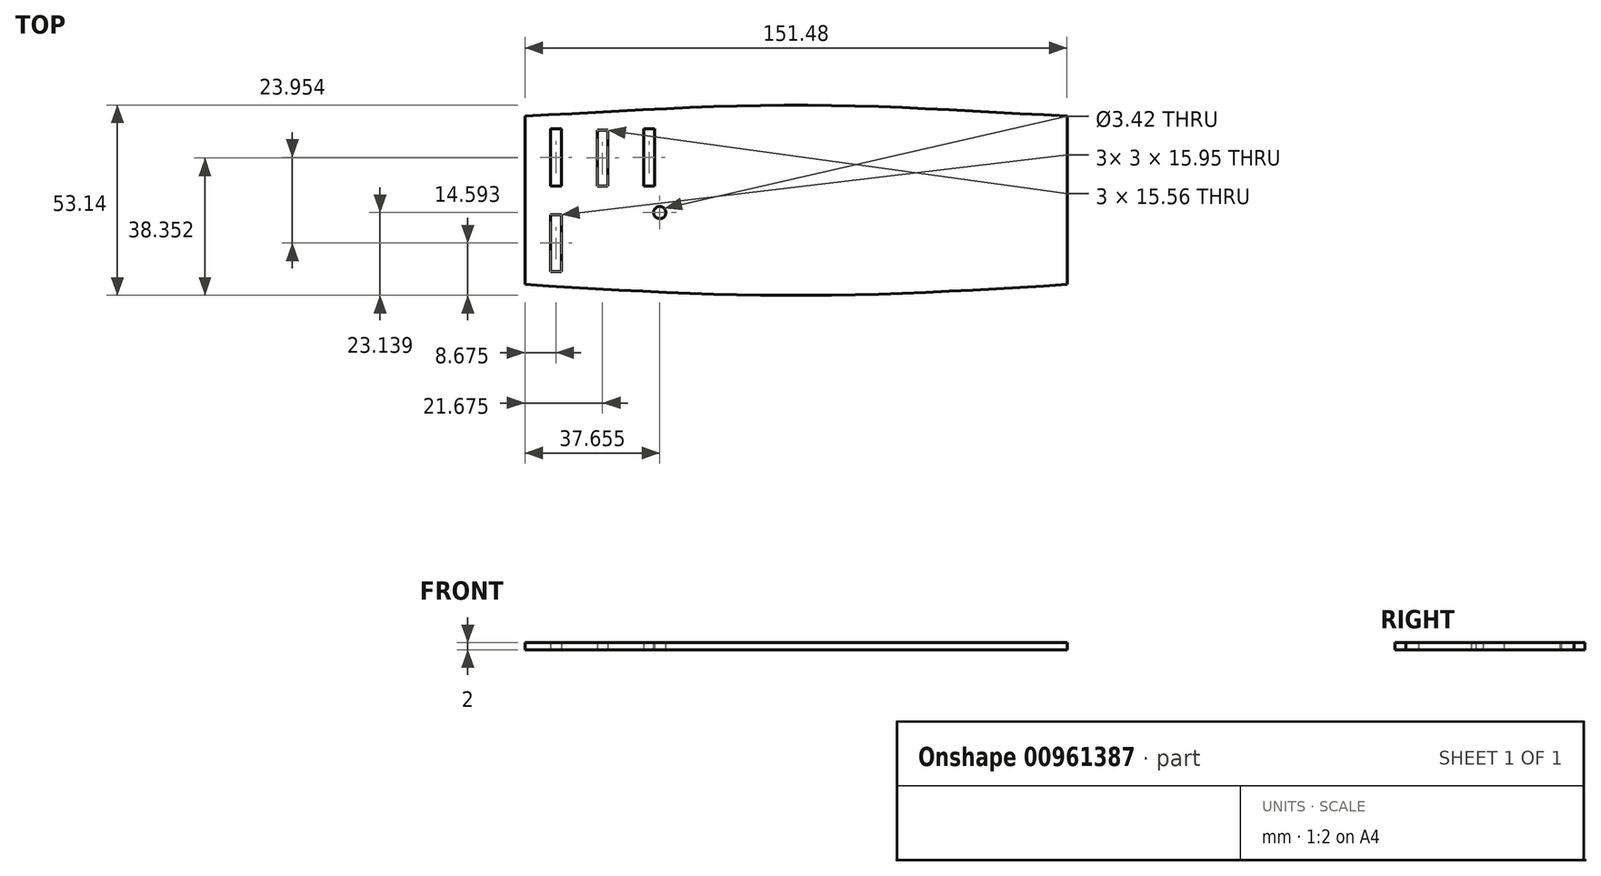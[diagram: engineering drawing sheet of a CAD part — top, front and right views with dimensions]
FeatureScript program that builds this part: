
annotation { "Feature Type Name" : "Feature", "Feature Type Description" : "" }
export const myFeature = defineFeature(function(context is Context, id is Id, definition is map)
    precondition{}
    {
        {
            var Q0;
            Q0=qCreatedBy(makeId("Top.planeOp"),FACE);
            var sketch = newSketch(context, id + "F0", { "sketchPlane" : qUnion([Q0])});
            skLineSegment(sketch, "E0.left", {"start": v(-75.74, 23.5) * mm, "end": v(-75.74, -23.5) * mm});
            skLineSegment(sketch, "E0.right", {"start": v(75.74, 23.5) * mm, "end": v(75.74, -23.5) * mm});
            skPoint(sketch, "E0.middle", {"position": v(0, 0) * mm});
            skFitSpline(sketch, "E1", {"points": [v(-75.74, -23.5) * mm, v(0, -26.57) * mm, v(75.74, -23.5) * mm], "startDerivative": vector(151.49, -9.97) * mm, "endDerivative": vector(151.49, 9.97) * mm});
            skFitSpline(sketch, "E2", {"points": [v(-75.74, 23.5) * mm, v(0, 26.57) * mm, v(75.74, 23.5) * mm], "startDerivative": vector(151.49, 7.52) * mm, "endDerivative": vector(151.49, -7.52) * mm});
            skLineSegment(sketch, "E3.bottom", {"start": v(-68.57, 19.95) * mm, "end": v(-65.57, 19.95) * mm});
            skLineSegment(sketch, "E3.top", {"start": v(-68.57, 4) * mm, "end": v(-65.57, 4) * mm});
            skLineSegment(sketch, "E3.left", {"start": v(-68.57, 19.95) * mm, "end": v(-68.57, 4) * mm});
            skLineSegment(sketch, "E3.right", {"start": v(-65.57, 19.95) * mm, "end": v(-65.57, 4) * mm});
            skLineSegment(sketch, "E4.bottom", {"start": v(-55.57, 19.56) * mm, "end": v(-52.57, 19.56) * mm});
            skLineSegment(sketch, "E4.top", {"start": v(-55.57, 4) * mm, "end": v(-52.57, 4) * mm});
            skLineSegment(sketch, "E4.left", {"start": v(-55.57, 19.56) * mm, "end": v(-55.57, 4) * mm});
            skLineSegment(sketch, "E4.right", {"start": v(-52.57, 19.56) * mm, "end": v(-52.57, 4) * mm});
            skLineSegment(sketch, "E5.bottom", {"start": v(-42.57, 19.95) * mm, "end": v(-39.57, 19.95) * mm});
            skLineSegment(sketch, "E5.top", {"start": v(-42.57, 4) * mm, "end": v(-39.57, 4) * mm});
            skLineSegment(sketch, "E5.left", {"start": v(-42.57, 19.95) * mm, "end": v(-42.57, 4) * mm});
            skLineSegment(sketch, "E5.right", {"start": v(-39.57, 19.95) * mm, "end": v(-39.57, 4) * mm});
            skLineSegment(sketch, "E6.bottom", {"start": v(-68.57, -4) * mm, "end": v(-65.57, -4) * mm});
            skLineSegment(sketch, "E6.top", {"start": v(-68.57, -19.95) * mm, "end": v(-65.57, -19.95) * mm});
            skLineSegment(sketch, "E6.left", {"start": v(-68.57, -4) * mm, "end": v(-68.57, -19.95) * mm});
            skLineSegment(sketch, "E6.right", {"start": v(-65.57, -4) * mm, "end": v(-65.57, -19.95) * mm});
            skPoint(sketch, "E7.endSnap0", {"position": v(-75.74, 0) * mm});
            skSolve(sketch);
        }
        {
            var Q0;
            Q0 = qSketchRegion(id + "F0", true);
            extrude(context, id + "F1", {"entities" : qUnion([Q0]), "depth" : 2 * mm, "offsetDistance" : 25 * mm});
        }
        {
            var Q0;
            Q0=makeQuery(id+"F1.opExtrude","CAP_FACE",FACE,{"disambiguationData":[OSD([sQuery(id+"F0.wireOp",EDGE,"E0.left"),sQuery(id+"F0.wireOp",EDGE,"E0.right"),sQuery(id+"F0.wireOp",EDGE,"E1"),sQuery(id+"F0.wireOp",EDGE,"E2"),sQuery(id+"F0.wireOp",EDGE,"E3.bottom"),sQuery(id+"F0.wireOp",EDGE,"E3.top"),sQuery(id+"F0.wireOp",EDGE,"E3.left"),sQuery(id+"F0.wireOp",EDGE,"E3.right"),sQuery(id+"F0.wireOp",EDGE,"E4.bottom"),sQuery(id+"F0.wireOp",EDGE,"E4.top"),sQuery(id+"F0.wireOp",EDGE,"E4.left"),sQuery(id+"F0.wireOp",EDGE,"E4.right"),sQuery(id+"F0.wireOp",EDGE,"E5.bottom"),sQuery(id+"F0.wireOp",EDGE,"E5.top"),sQuery(id+"F0.wireOp",EDGE,"E5.left"),sQuery(id+"F0.wireOp",EDGE,"E5.right"),sQuery(id+"F0.wireOp",EDGE,"E6.bottom"),sQuery(id+"F0.wireOp",EDGE,"E6.top"),sQuery(id+"F0.wireOp",EDGE,"E6.left"),sQuery(id+"F0.wireOp",EDGE,"E6.right")])],"isStart":false});
            var sketch = newSketch(context, id + "F2", { "sketchPlane" : qUnion([Q0])});
            skCircle(sketch, "E8", {"center": v(-38.08, -3.43) * mm, "radius": 1.7 * mm});
            skCircle(sketch, "E9", {"center": v(-38.08, -3.43) * mm, "radius": 3.6 * mm});
            skSolve(sketch);
        }
        {
            var Q0;
            Q0=makeQuery(id+"F2.imprint","IMPRINT",FACE,{"disambiguationData":[TD([[makeQuery(id+"F2.imprint","IMPRINT",EDGE,{"derivedFrom":sQuery(id+"F2.wireOp",EDGE,"E8")}),1.0]])]});
            extrude(context, id + "F3", {"entities" : qUnion([Q0]), "operationType" : NewBodyOperationType.REMOVE, "oppositeDirection" : true, "depth" : 25 * mm, "offsetDistance" : 25 * mm});
        }
    });
